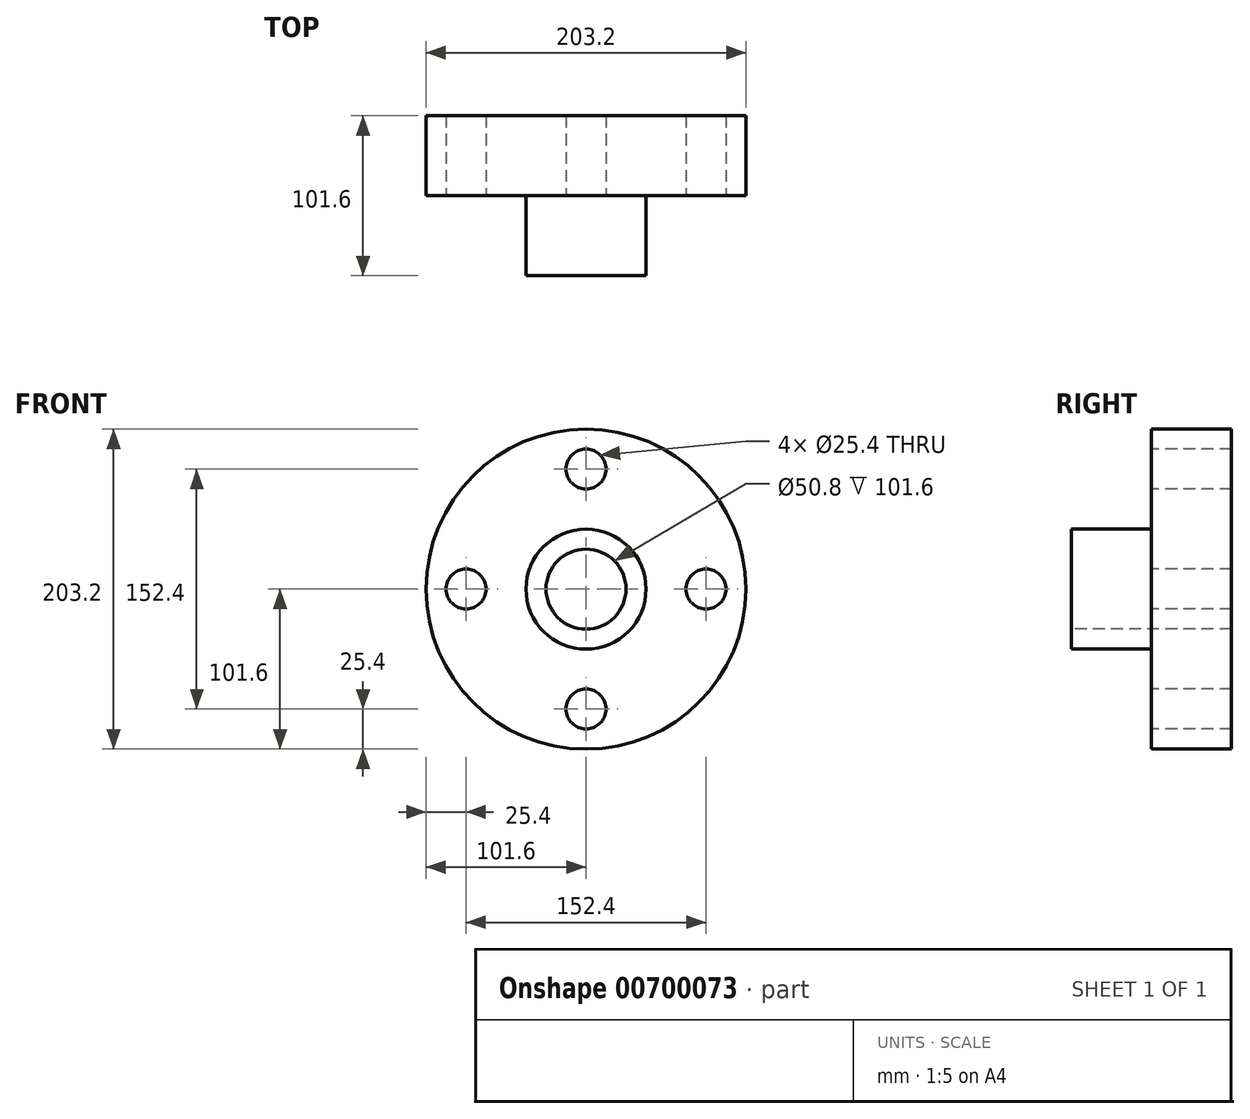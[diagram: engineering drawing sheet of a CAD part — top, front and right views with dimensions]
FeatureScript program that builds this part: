
annotation { "Feature Type Name" : "Feature", "Feature Type Description" : "" }
export const myFeature = defineFeature(function(context is Context, id is Id, definition is map)
    precondition{}
    {
        {
            var Q0;
            Q0=qCreatedBy(makeId("Front.planeOp"),FACE);
            var sketch = newSketch(context, id + "F0", { "sketchPlane" : qUnion([Q0])});
            skCircle(sketch, "E0", {"center": v(0, 0) * mm, "radius": 101.6 * mm});
            skSolve(sketch);
        }
        {
            var Q0;
            Q0=makeQuery(id+"F0.imprint","IMPRINT",FACE,{"disambiguationData":[TD([[makeQuery(id+"F0.imprint","IMPRINT",EDGE,{"derivedFrom":sQuery(id+"F0.wireOp",EDGE,"E0")}),1.0]])]});
            extrude(context, id + "F1", {"entities" : qUnion([Q0]), "depth" : 50.8 * mm, "offsetDistance" : 25.4 * mm});
        }
        {
            var Q0;
            Q0=makeQuery(id+"F1.opExtrude","CAP_FACE",FACE,{"disambiguationData":[OSD([sQuery(id+"F0.wireOp",EDGE,"E0")])],"isStart":false});
            var sketch = newSketch(context, id + "F2", { "sketchPlane" : qUnion([Q0])});
            skCircle(sketch, "E1", {"center": v(0, 0) * mm, "radius": 38.1 * mm});
            skSolve(sketch);
        }
        {
            var Q0;
            Q0 = qSketchRegion(id + "F2", true);
            extrude(context, id + "F3", {"entities" : qUnion([Q0]), "operationType" : NewBodyOperationType.ADD, "depth" : 50.8 * mm, "offsetDistance" : 25.4 * mm});
        }
        {
            var Q0;
            Q0=makeQuery(id+"F3.opExtrude","CAP_FACE",FACE,{"disambiguationData":[OSD([sQuery(id+"F2.wireOp",EDGE,"E1")])],"isStart":false});
            var sketch = newSketch(context, id + "F4", { "sketchPlane" : qUnion([Q0])});
            skCircle(sketch, "E2", {"center": v(0, 0) * mm, "radius": 25.4 * mm});
            skSolve(sketch);
        }
        {
            var Q0;
            Q0 = qSketchRegion(id + "F4", true);
            extrude(context, id + "F5", {"entities" : qUnion([Q0]), "operationType" : NewBodyOperationType.REMOVE, "oppositeDirection" : true, "depth" : 148.08 * mm, "offsetDistance" : 25.4 * mm});
        }
        {
            var Q0;
            Q0=makeQuery(id+"F1.opExtrude","CAP_FACE",FACE,{"disambiguationData":[OSD([sQuery(id+"F0.wireOp",EDGE,"E0")])],"isStart":false});
            var sketch = newSketch(context, id + "F6", { "sketchPlane" : qUnion([Q0])});
            skLineSegment(sketch, "E3", {"start": v(0, 0) * mm, "end": v(0, 76.2) * mm, "construction": true});
            skLineSegment(sketch, "E4", {"start": v(0, 76.2) * mm, "end": v(0, 0) * mm, "construction": true});
            skLineSegment(sketch, "E5", {"start": v(0, 0) * mm, "end": v(76.2, 0) * mm, "construction": true});
            skLineSegment(sketch, "E6", {"start": v(76.2, 0) * mm, "end": v(0, 0) * mm, "construction": true});
            skLineSegment(sketch, "E7", {"start": v(0, 0) * mm, "end": v(0, -76.2) * mm, "construction": true});
            skLineSegment(sketch, "E8", {"start": v(0, -76.2) * mm, "end": v(0, 0) * mm, "construction": true});
            skLineSegment(sketch, "E9", {"start": v(0, 0) * mm, "end": v(-76.2, 0) * mm, "construction": true});
            skCircle(sketch, "E10", {"center": v(0, 76.2) * mm, "radius": 12.7 * mm});
            skCircle(sketch, "E11", {"center": v(76.2, 0) * mm, "radius": 12.7 * mm});
            skCircle(sketch, "E12", {"center": v(0, -76.2) * mm, "radius": 12.7 * mm});
            skCircle(sketch, "E13", {"center": v(-76.2, 0) * mm, "radius": 12.7 * mm});
            skSolve(sketch);
        }
        {
            var Q0;
            Q0 = qSketchRegion(id + "F6", true);
            extrude(context, id + "F7", {"entities" : qUnion([Q0]), "operationType" : NewBodyOperationType.REMOVE, "oppositeDirection" : true, "depth" : 95.76 * mm, "offsetDistance" : 25.4 * mm});
        }
    });
